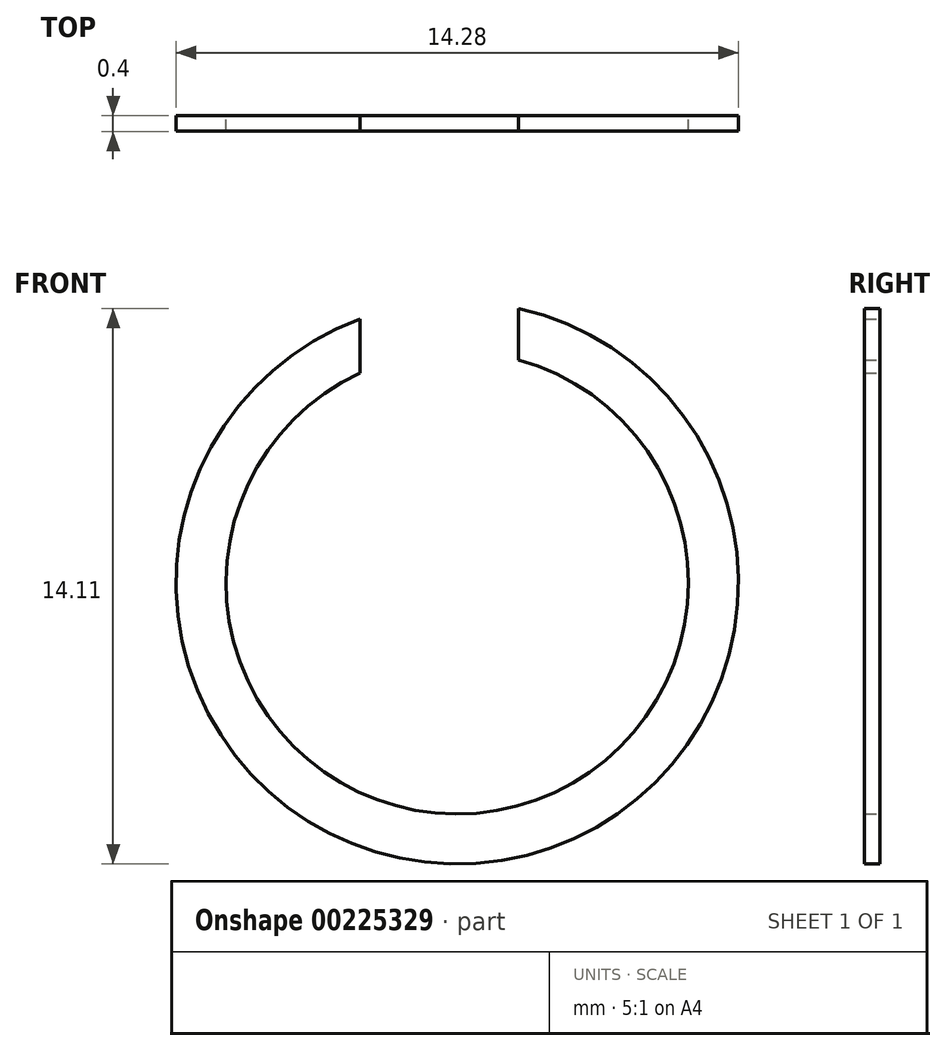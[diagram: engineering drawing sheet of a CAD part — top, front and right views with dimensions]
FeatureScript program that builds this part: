
annotation { "Feature Type Name" : "Feature", "Feature Type Description" : "" }
export const myFeature = defineFeature(function(context is Context, id is Id, definition is map)
    precondition{}
    {
        {
            var Q0;
            Q0=qCreatedBy(makeId("Front.planeOp"),FACE);
            var sketch = newSketch(context, id + "F0", { "sketchPlane" : qUnion([Q0])});
            skArc(sketch, "E0", {"start": v(-2.47, 6.7) * mm, "mid": v(0.48, -7.13) * mm, "end": v(1.55, 6.97) * mm});
            skArc(sketch, "E1.0", {"start": v(-2.47, 5.33) * mm, "mid": v(0.49, -5.85) * mm, "end": v(1.55, 5.67) * mm});
            skLineSegment(sketch, "E2", {"start": v(1.55, 5.67) * mm, "end": v(1.55, 6.97) * mm});
            skLineSegment(sketch, "E3", {"start": v(-2.47, 5.33) * mm, "end": v(-2.47, 6.7) * mm});
            skSolve(sketch);
        }
        {
            var Q0;
            Q0 = qSketchRegion(id + "F0", true);
            extrude(context, id + "F1", {"entities" : qUnion([Q0]), "depth" : 0.4 * mm});
        }
    });
